# Revit family: Sink-Bar-KOHLER-Vault-K-3840
name_source: partatom
category: Plumbing Fixtures
revit_build: Autodesk Revit 2015 (Build: 20140606_1530(x64)
units: mm (PartAtom-declared; Revit-internal decimal feet)

## types (3) — shared parameters
ADA Compliant = Yes
Assembly Code = D2010400
CW Connection = No
Cold Water Inlet = Cold Water Inlet
Date Modified = 04/23/2019
Default Elevation = 36"
Drain Included = No
Finish = Kohler-Metal-NA-Stainless
HW Connection = No
Height = 9 5/16"
Hot Water Inlet = Hot Water Inlet
Length = 15"
Manufacturer = KOHLER Co.
MasterFormat 1995 = 15410
MasterFormat 2004 = 22.41.16
Material = 18-Gauge Stainless Steel
Product Documentation Link = https://www.us.kohler.com
Product Name = Vault
Product Page URL = http://www.us.kohler.com
URL = https://www.us.kohler.com
Vent Connection = No
Waste Connection = Yes
Waste Water Outlet = Waste Water Outlet
WaterSense Certified = No
Width = 15"

## per-type parameters (varying)
| type | -1 | 2 Faucet Holes | 3 Faucet Holes | Description | Faucet Hole Spacing | Model | Type |
| 1 Faucet Holes, NA-Stainless Steel | Yes | No | No | 15inch x 15inch x 9-5/16inch top-/under-mount bar sink with single faucet hole | 0" | K-3840-1-NA | 1 |
| 2 Faucet Holes, NA-Stainless Steel | No | Yes | No | 15inch x 15inch x 9-5/16inch top-/under-mount bar sink with 2 faucet holes | 4" | K-3840-2-NA | 2 |
| 3 Faucet Holes, NA-Stainless Steel | No | No | Yes | 12-1/4inch x 9-9/16inch x 9inch top-/under-mount bar sink with 3 faucet holes | 8" | K-3840-3-NA | 3 |

## geometry (parser evidence)
native form markers: Sweep x4
no freeform markers — native parametric forms only
